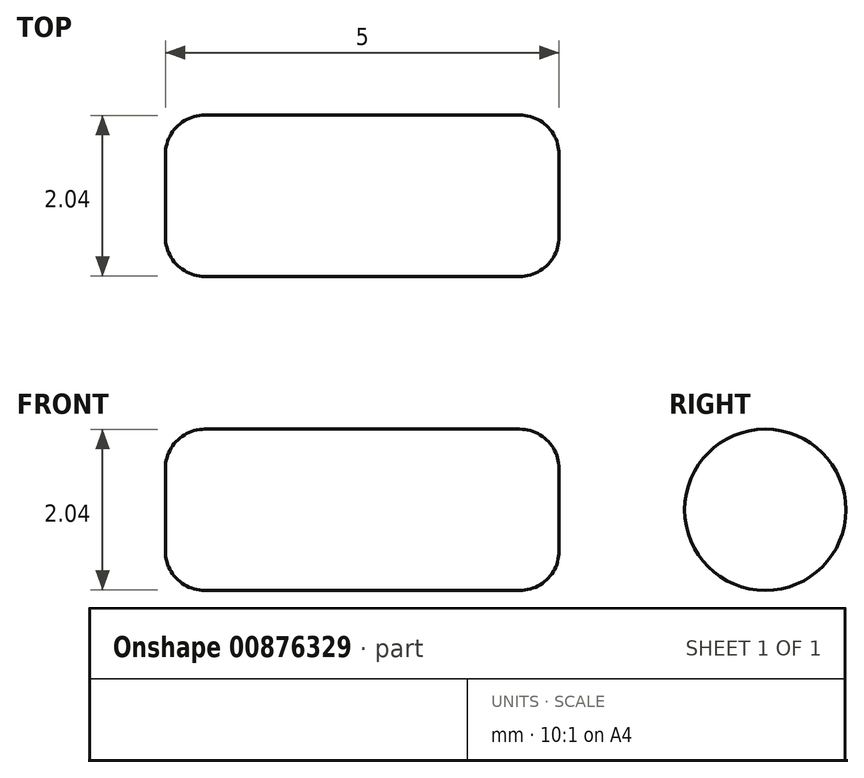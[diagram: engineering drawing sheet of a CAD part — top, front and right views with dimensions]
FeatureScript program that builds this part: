
annotation { "Feature Type Name" : "Feature", "Feature Type Description" : "" }
export const myFeature = defineFeature(function(context is Context, id is Id, definition is map)
    precondition{}
    {
        {
            var Q0;
            Q0=qCreatedBy(makeId("Right.planeOp"),FACE);
            var sketch = newSketch(context, id + "F0", { "sketchPlane" : qUnion([Q0])});
            skCircle(sketch, "E0", {"center": v(0, 0) * mm, "radius": 1.02 * mm});
            skSolve(sketch);
        }
        {
            var Q0;
            Q0=qCreatedBy(makeId("Front.planeOp"),FACE);
            var sketch = newSketch(context, id + "F1", { "sketchPlane" : qUnion([Q0])});
            skLineSegment(sketch, "E1", {"start": v(0, 0) * mm, "end": v(-5, 0) * mm});
            skSolve(sketch);
        }
        {
            var Q0;
            Q0=makeQuery(id+"F0.imprint","IMPRINT",FACE,{"disambiguationData":[TD([[makeQuery(id+"F0.imprint","IMPRINT",EDGE,{"derivedFrom":sQuery(id+"F0.wireOp",EDGE,"E0")}),1.0]])]});
            var Q1;
            Q1=sQuery(id+"F1.wireOp",EDGE,"E1");
            sweep(context, id + "F2", {"profiles" : qUnion([Q0]), "path" : qUnion([Q1])});
        }
        {
            var Q0;
            Q0=makeQuery(id+"F2.opSweep","CAP_EDGE",EDGE,{"disambiguationData":[OSD([sQuery(id+"F0.wireOp",EDGE,"E0"),sQuery(id+"F1.wireOp",VERTEX,"E1.end")])],"isStart":false});
            var Q1;
            Q1=makeQuery(id+"F2.opSweep","CAP_EDGE",EDGE,{"disambiguationData":[OSD([sQuery(id+"F0.wireOp",EDGE,"E0"),sQuery(id+"F1.wireOp",VERTEX,"E1.start")])],"isStart":true});
            fillet(context, id + "F3", {"entities" : qUnion([Q0, Q1]), "radius" : 0.5 * mm, "tangentPropagation" : true, "allowEdgeOverflow" : false});
        }
    });
